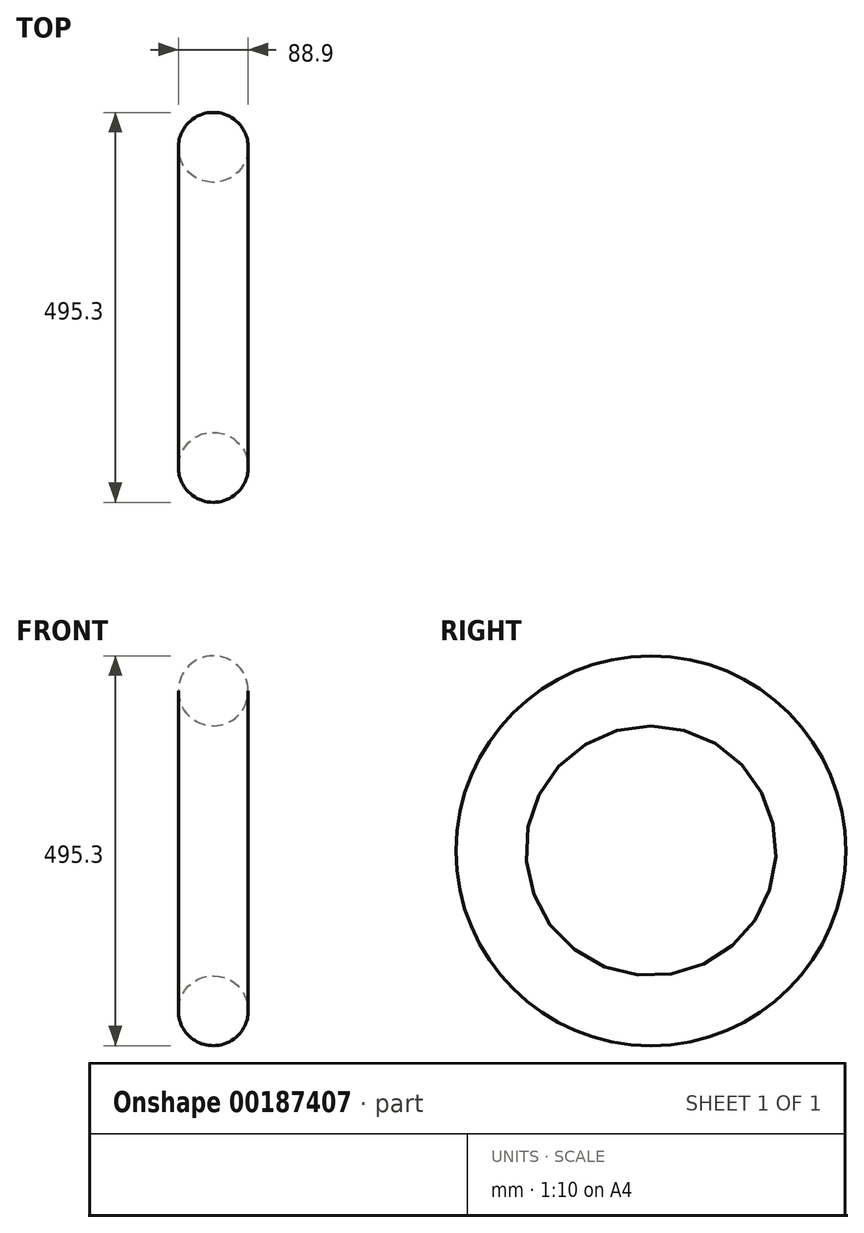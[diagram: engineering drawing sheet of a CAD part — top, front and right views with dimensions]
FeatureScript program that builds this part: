
annotation { "Feature Type Name" : "Feature", "Feature Type Description" : "" }
export const myFeature = defineFeature(function(context is Context, id is Id, definition is map)
    precondition{}
    {
        {
            var Q0;
            Q0=qCreatedBy(makeId("Top.planeOp"),FACE);
            var sketch = newSketch(context, id + "F0", { "sketchPlane" : qUnion([Q0])});
            skLineSegment(sketch, "E0", {"start": v(0, 0) * mm, "end": v(0, 203.2) * mm});
            skCircle(sketch, "E1", {"center": v(0, 203.2) * mm, "radius": 44.45 * mm});
            skSolve(sketch);
        }
        {
            var Q0;
            Q0=qCreatedBy(makeId("Front.planeOp"),FACE);
            var sketch = newSketch(context, id + "F1", { "sketchPlane" : qUnion([Q0])});
            skLineSegment(sketch, "E2", {"start": v(0, 0) * mm, "end": v(76.2, 0) * mm});
            skSolve(sketch);
        }
        {
            var Q0;
            Q0=makeQuery(id+"F0.imprint","IMPRINT",FACE,{"disambiguationData":[TD([[makeQuery(id+"F0.imprint","IMPRINT",EDGE,{"derivedFrom":sQuery(id+"F0.wireOp",EDGE,"E1")}),1.0]])]});
            var Q1;
            Q1=sQuery(id+"F1.wireOp",EDGE,"E2");
            revolve(context, id + "F2", {"entities" : qUnion([Q0]), "axis" : qUnion([Q1]), "revolveType" : RevolveType.FULL});
        }
    });
